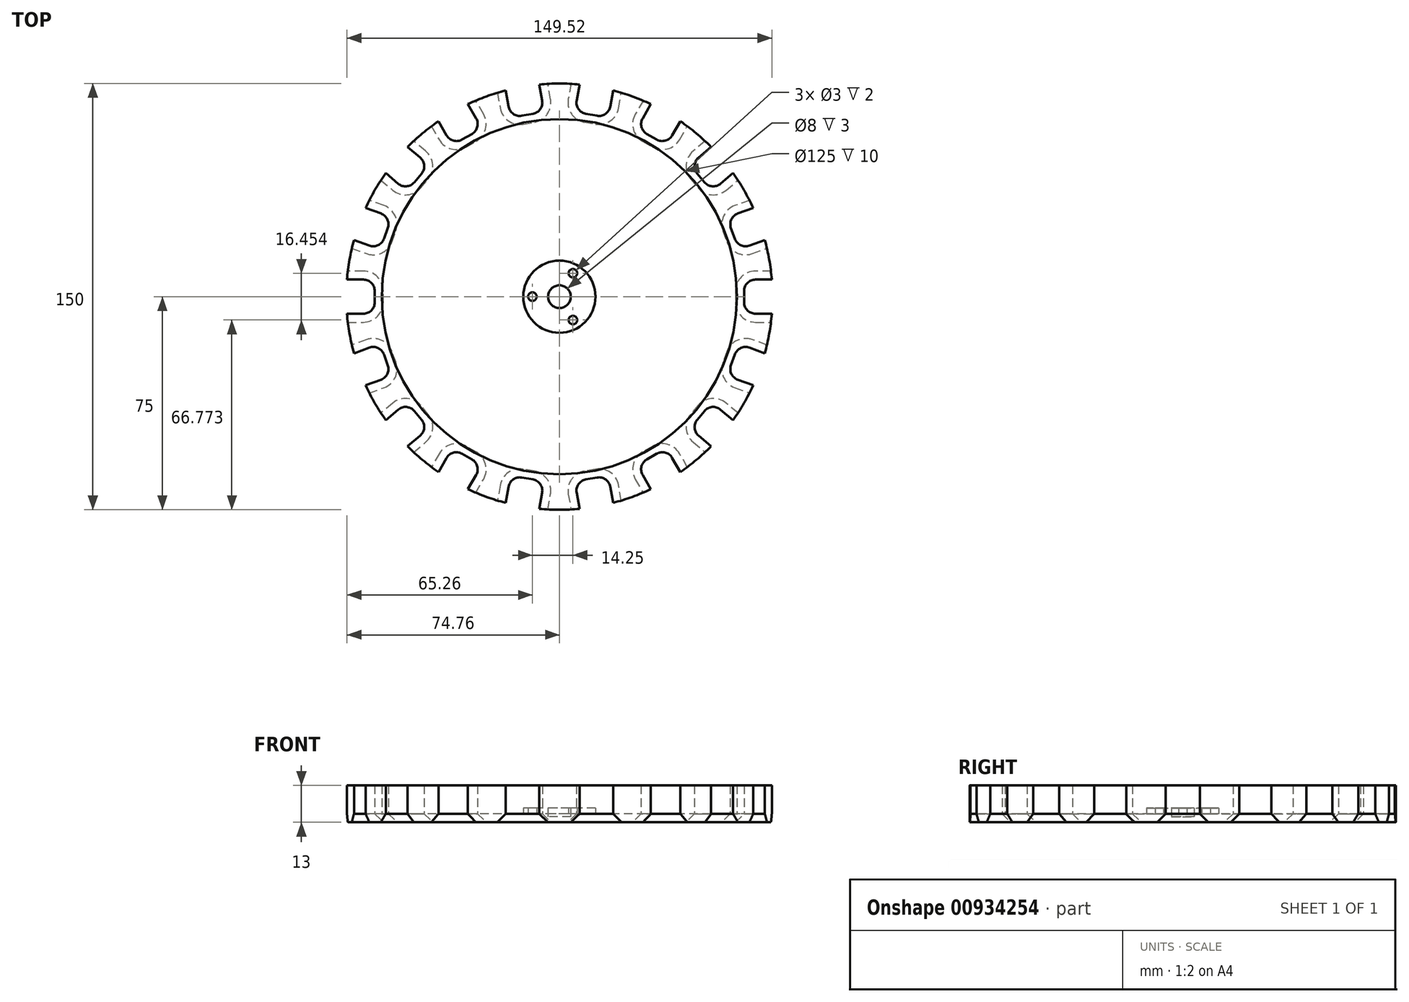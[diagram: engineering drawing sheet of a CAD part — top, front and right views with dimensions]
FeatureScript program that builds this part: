
annotation { "Feature Type Name" : "Feature", "Feature Type Description" : "" }
export const myFeature = defineFeature(function(context is Context, id is Id, definition is map)
    precondition{}
    {
        {
            var Q0;
            Q0=qCreatedBy(makeId("Top.planeOp"),FACE);
            var sketch = newSketch(context, id + "F0", { "sketchPlane" : qUnion([Q0])});
            skCircle(sketch, "E0", {"center": v(0, 0) * mm, "radius": 75 * mm});
            skCircle(sketch, "E1", {"center": v(0, 0) * mm, "radius": 62.5 * mm});
            skLineSegment(sketch, "E2", {"start": v(0, 0) * mm, "end": v(-124.02, 0) * mm, "construction": true});
            skPoint(sketch, "E3", {"position": v(-75, 0) * mm});
            skLineSegment(sketch, "E4.bottom", {"start": v(-75, -6) * mm, "end": v(-69, -6) * mm});
            skLineSegment(sketch, "E4.top", {"start": v(-75, 6) * mm, "end": v(-69, 6) * mm});
            skLineSegment(sketch, "E4.left", {"start": v(-75, -6) * mm, "end": v(-75, 6) * mm});
            skLineSegment(sketch, "E4.right", {"start": v(-65, -2) * mm, "end": v(-65, 2) * mm});
            skPoint(sketch, "E4.middle", {"position": v(-70, 0) * mm});
            skPoint(sketch, "E5.visualSharp", {"position": v(-65, 6) * mm});
            skArc(sketch, "E5.filletArc", {"start": v(-65, 2) * mm, "mid": v(-66.17, 4.83) * mm, "end": v(-69, 6) * mm});
            skPoint(sketch, "E6.visualSharp", {"position": v(-65, -6) * mm});
            skArc(sketch, "E6.filletArc", {"start": v(-69, -6) * mm, "mid": v(-66.17, -4.83) * mm, "end": v(-65, -2) * mm});
            skPoint(sketch, "E7.center", {"position": v(1.56, 0) * mm});
            skCircle(sketch, "E8", {"center": v(0, 0) * mm, "radius": 4 * mm});
            skCircle(sketch, "E9", {"center": v(0, 0) * mm, "radius": 12.7 * mm});
            skCircle(sketch, "E10", {"center": v(0, 0) * mm, "radius": 9.5 * mm, "construction": true});
            skCircle(sketch, "E11", {"center": v(-9.5, 0) * mm, "radius": 1.5 * mm});
            skCircle(sketch, "E12.1.0", {"center": v(-4.75, -8.23) * mm, "radius": 1.5 * mm});
            skCircle(sketch, "E12.2.0", {"center": v(4.75, -8.23) * mm, "radius": 1.5 * mm});
            skCircle(sketch, "E12.3.0", {"center": v(9.5, 0) * mm, "radius": 1.5 * mm});
            skCircle(sketch, "E12.4.0", {"center": v(4.75, 8.23) * mm, "radius": 1.5 * mm});
            skCircle(sketch, "E12.5.0", {"center": v(-4.75, 8.23) * mm, "radius": 1.5 * mm});
            skPoint(sketch, "E13.1.0", {"position": v(-63.13, -16.6) * mm});
            skPoint(sketch, "E13.1.1", {"position": v(-70.48, -25.65) * mm});
            skPoint(sketch, "E13.1.2", {"position": v(-59.03, -27.87) * mm});
            skPoint(sketch, "E13.1.3", {"position": v(-65.78, -23.94) * mm});
            skArc(sketch, "E13.1.4", {"start": v(-62.79, -29.24) * mm, "mid": v(-60.53, -27.17) * mm, "end": v(-60.4, -24.11) * mm});
            skArc(sketch, "E13.1.5", {"start": v(-61.76, -20.35) * mm, "mid": v(-63.83, -18.1) * mm, "end": v(-66.9, -17.96) * mm});
            skLineSegment(sketch, "E13.1.6", {"start": v(-68.42, -31.29) * mm, "end": v(-72.53, -20.01) * mm});
            skLineSegment(sketch, "E13.1.7", {"start": v(-60.4, -24.11) * mm, "end": v(-61.76, -20.35) * mm});
            skLineSegment(sketch, "E13.1.8", {"start": v(-72.53, -20.01) * mm, "end": v(-66.9, -17.96) * mm});
            skLineSegment(sketch, "E13.1.9", {"start": v(-68.42, -31.29) * mm, "end": v(-62.79, -29.24) * mm});
            skPoint(sketch, "E13.2.0", {"position": v(-53.65, -37.18) * mm});
            skPoint(sketch, "E13.2.1", {"position": v(-57.45, -48.2) * mm});
            skPoint(sketch, "E13.2.2", {"position": v(-45.94, -46.38) * mm});
            skPoint(sketch, "E13.2.3", {"position": v(-53.62, -45) * mm});
            skArc(sketch, "E13.2.4", {"start": v(-49, -48.95) * mm, "mid": v(-47.59, -46.23) * mm, "end": v(-48.5, -43.31) * mm});
            skArc(sketch, "E13.2.5", {"start": v(-51.08, -40.25) * mm, "mid": v(-53.8, -38.84) * mm, "end": v(-56.71, -39.76) * mm});
            skLineSegment(sketch, "E13.2.6", {"start": v(-53.6, -52.8) * mm, "end": v(-61.31, -43.61) * mm});
            skLineSegment(sketch, "E13.2.7", {"start": v(-48.5, -43.31) * mm, "end": v(-51.08, -40.25) * mm});
            skLineSegment(sketch, "E13.2.8", {"start": v(-61.31, -43.61) * mm, "end": v(-56.71, -39.76) * mm});
            skLineSegment(sketch, "E13.2.9", {"start": v(-53.6, -52.8) * mm, "end": v(-49, -48.95) * mm});
            skPoint(sketch, "E13.3.0", {"position": v(-37.7, -53.3) * mm});
            skPoint(sketch, "E13.3.1", {"position": v(-37.5, -64.95) * mm});
            skPoint(sketch, "E13.3.2", {"position": v(-27.3, -59.3) * mm});
            skPoint(sketch, "E13.3.3", {"position": v(-35, -60.62) * mm});
            skArc(sketch, "E13.3.4", {"start": v(-29.3, -62.76) * mm, "mid": v(-28.9, -59.72) * mm, "end": v(-30.77, -57.3) * mm});
            skArc(sketch, "E13.3.5", {"start": v(-34.23, -55.3) * mm, "mid": v(-37.27, -54.9) * mm, "end": v(-39.7, -56.76) * mm});
            skLineSegment(sketch, "E13.3.6", {"start": v(-32.3, -67.95) * mm, "end": v(-42.7, -61.95) * mm});
            skLineSegment(sketch, "E13.3.7", {"start": v(-30.77, -57.3) * mm, "end": v(-34.23, -55.3) * mm});
            skLineSegment(sketch, "E13.3.8", {"start": v(-42.7, -61.95) * mm, "end": v(-39.7, -56.76) * mm});
            skLineSegment(sketch, "E13.3.9", {"start": v(-32.3, -67.95) * mm, "end": v(-29.3, -62.76) * mm});
            skPoint(sketch, "E13.4.0", {"position": v(-17.2, -62.97) * mm});
            skPoint(sketch, "E13.4.1", {"position": v(-13.02, -73.86) * mm});
            skPoint(sketch, "E13.4.2", {"position": v(-5.38, -65.05) * mm});
            skPoint(sketch, "E13.4.3", {"position": v(-12.16, -68.94) * mm});
            skArc(sketch, "E13.4.4", {"start": v(-6.07, -69) * mm, "mid": v(-6.74, -66) * mm, "end": v(-9.32, -64.36) * mm});
            skArc(sketch, "E13.4.5", {"start": v(-13.26, -63.67) * mm, "mid": v(-16.25, -64.33) * mm, "end": v(-17.9, -66.9) * mm});
            skLineSegment(sketch, "E13.4.6", {"start": v(-7.11, -74.9) * mm, "end": v(-18.93, -72.82) * mm});
            skLineSegment(sketch, "E13.4.7", {"start": v(-9.32, -64.36) * mm, "end": v(-13.26, -63.67) * mm});
            skLineSegment(sketch, "E13.4.8", {"start": v(-18.93, -72.82) * mm, "end": v(-17.9, -66.9) * mm});
            skLineSegment(sketch, "E13.4.9", {"start": v(-7.11, -74.9) * mm, "end": v(-6.07, -69) * mm});
            skPoint(sketch, "E13.5.0", {"position": v(5.38, -65.05) * mm});
            skPoint(sketch, "E13.5.1", {"position": v(13.02, -73.86) * mm});
            skPoint(sketch, "E13.5.2", {"position": v(17.2, -62.97) * mm});
            skPoint(sketch, "E13.5.3", {"position": v(12.16, -68.94) * mm});
            skArc(sketch, "E13.5.4", {"start": v(17.9, -66.9) * mm, "mid": v(16.25, -64.33) * mm, "end": v(13.26, -63.67) * mm});
            skArc(sketch, "E13.5.5", {"start": v(9.32, -64.36) * mm, "mid": v(6.74, -66) * mm, "end": v(6.07, -69) * mm});
            skLineSegment(sketch, "E13.5.6", {"start": v(18.93, -72.82) * mm, "end": v(7.11, -74.9) * mm});
            skLineSegment(sketch, "E13.5.7", {"start": v(13.26, -63.67) * mm, "end": v(9.32, -64.36) * mm});
            skLineSegment(sketch, "E13.5.8", {"start": v(7.11, -74.9) * mm, "end": v(6.07, -69) * mm});
            skLineSegment(sketch, "E13.5.9", {"start": v(18.93, -72.82) * mm, "end": v(17.9, -66.9) * mm});
            skPoint(sketch, "E13.6.0", {"position": v(27.3, -59.3) * mm});
            skPoint(sketch, "E13.6.1", {"position": v(37.5, -64.95) * mm});
            skPoint(sketch, "E13.6.2", {"position": v(37.7, -53.3) * mm});
            skPoint(sketch, "E13.6.3", {"position": v(35, -60.62) * mm});
            skArc(sketch, "E13.6.4", {"start": v(39.7, -56.76) * mm, "mid": v(37.27, -54.9) * mm, "end": v(34.23, -55.3) * mm});
            skArc(sketch, "E13.6.5", {"start": v(30.77, -57.3) * mm, "mid": v(28.9, -59.72) * mm, "end": v(29.3, -62.76) * mm});
            skLineSegment(sketch, "E13.6.6", {"start": v(42.7, -61.95) * mm, "end": v(32.3, -67.95) * mm});
            skLineSegment(sketch, "E13.6.7", {"start": v(34.23, -55.3) * mm, "end": v(30.77, -57.3) * mm});
            skLineSegment(sketch, "E13.6.8", {"start": v(32.3, -67.95) * mm, "end": v(29.3, -62.76) * mm});
            skLineSegment(sketch, "E13.6.9", {"start": v(42.7, -61.95) * mm, "end": v(39.7, -56.76) * mm});
            skPoint(sketch, "E13.7.0", {"position": v(45.94, -46.38) * mm});
            skPoint(sketch, "E13.7.1", {"position": v(57.45, -48.2) * mm});
            skPoint(sketch, "E13.7.2", {"position": v(53.65, -37.18) * mm});
            skPoint(sketch, "E13.7.3", {"position": v(53.62, -45) * mm});
            skArc(sketch, "E13.7.4", {"start": v(56.71, -39.76) * mm, "mid": v(53.8, -38.84) * mm, "end": v(51.08, -40.25) * mm});
            skArc(sketch, "E13.7.5", {"start": v(48.5, -43.31) * mm, "mid": v(47.59, -46.23) * mm, "end": v(49, -48.95) * mm});
            skLineSegment(sketch, "E13.7.6", {"start": v(61.31, -43.61) * mm, "end": v(53.6, -52.8) * mm});
            skLineSegment(sketch, "E13.7.7", {"start": v(51.08, -40.25) * mm, "end": v(48.5, -43.31) * mm});
            skLineSegment(sketch, "E13.7.8", {"start": v(53.6, -52.8) * mm, "end": v(49, -48.95) * mm});
            skLineSegment(sketch, "E13.7.9", {"start": v(61.31, -43.61) * mm, "end": v(56.71, -39.76) * mm});
            skPoint(sketch, "E13.8.0", {"position": v(59.03, -27.87) * mm});
            skPoint(sketch, "E13.8.1", {"position": v(70.48, -25.65) * mm});
            skPoint(sketch, "E13.8.2", {"position": v(63.13, -16.6) * mm});
            skPoint(sketch, "E13.8.3", {"position": v(65.78, -23.94) * mm});
            skArc(sketch, "E13.8.4", {"start": v(66.9, -17.96) * mm, "mid": v(63.83, -18.1) * mm, "end": v(61.76, -20.35) * mm});
            skArc(sketch, "E13.8.5", {"start": v(60.4, -24.11) * mm, "mid": v(60.53, -27.17) * mm, "end": v(62.79, -29.24) * mm});
            skLineSegment(sketch, "E13.8.6", {"start": v(72.53, -20.01) * mm, "end": v(68.42, -31.29) * mm});
            skLineSegment(sketch, "E13.8.7", {"start": v(61.76, -20.35) * mm, "end": v(60.4, -24.11) * mm});
            skLineSegment(sketch, "E13.8.8", {"start": v(68.42, -31.29) * mm, "end": v(62.79, -29.24) * mm});
            skLineSegment(sketch, "E13.8.9", {"start": v(72.53, -20.01) * mm, "end": v(66.9, -17.96) * mm});
            skPoint(sketch, "E13.9.0", {"position": v(65, -6) * mm});
            skPoint(sketch, "E13.9.1", {"position": v(75, 0) * mm});
            skPoint(sketch, "E13.9.2", {"position": v(65, 6) * mm});
            skPoint(sketch, "E13.9.3", {"position": v(70, 0) * mm});
            skArc(sketch, "E13.9.4", {"start": v(69, 6) * mm, "mid": v(66.17, 4.83) * mm, "end": v(65, 2) * mm});
            skArc(sketch, "E13.9.5", {"start": v(65, -2) * mm, "mid": v(66.17, -4.83) * mm, "end": v(69, -6) * mm});
            skLineSegment(sketch, "E13.9.6", {"start": v(75, 6) * mm, "end": v(75, -6) * mm});
            skLineSegment(sketch, "E13.9.7", {"start": v(65, 2) * mm, "end": v(65, -2) * mm});
            skLineSegment(sketch, "E13.9.8", {"start": v(75, -6) * mm, "end": v(69, -6) * mm});
            skLineSegment(sketch, "E13.9.9", {"start": v(75, 6) * mm, "end": v(69, 6) * mm});
            skPoint(sketch, "E13.10.0", {"position": v(63.13, 16.6) * mm});
            skPoint(sketch, "E13.10.1", {"position": v(70.48, 25.65) * mm});
            skPoint(sketch, "E13.10.2", {"position": v(59.03, 27.87) * mm});
            skPoint(sketch, "E13.10.3", {"position": v(65.78, 23.94) * mm});
            skArc(sketch, "E13.10.4", {"start": v(62.79, 29.24) * mm, "mid": v(60.53, 27.17) * mm, "end": v(60.4, 24.11) * mm});
            skArc(sketch, "E13.10.5", {"start": v(61.76, 20.35) * mm, "mid": v(63.83, 18.1) * mm, "end": v(66.9, 17.96) * mm});
            skLineSegment(sketch, "E13.10.6", {"start": v(68.42, 31.29) * mm, "end": v(72.53, 20.01) * mm});
            skLineSegment(sketch, "E13.10.7", {"start": v(60.4, 24.11) * mm, "end": v(61.76, 20.35) * mm});
            skLineSegment(sketch, "E13.10.8", {"start": v(72.53, 20.01) * mm, "end": v(66.9, 17.96) * mm});
            skLineSegment(sketch, "E13.10.9", {"start": v(68.42, 31.29) * mm, "end": v(62.79, 29.24) * mm});
            skPoint(sketch, "E13.11.0", {"position": v(53.65, 37.18) * mm});
            skPoint(sketch, "E13.11.1", {"position": v(57.45, 48.2) * mm});
            skPoint(sketch, "E13.11.2", {"position": v(45.94, 46.38) * mm});
            skPoint(sketch, "E13.11.3", {"position": v(53.62, 45) * mm});
            skArc(sketch, "E13.11.4", {"start": v(49, 48.95) * mm, "mid": v(47.59, 46.23) * mm, "end": v(48.5, 43.31) * mm});
            skArc(sketch, "E13.11.5", {"start": v(51.08, 40.25) * mm, "mid": v(53.8, 38.84) * mm, "end": v(56.71, 39.76) * mm});
            skLineSegment(sketch, "E13.11.6", {"start": v(53.6, 52.8) * mm, "end": v(61.31, 43.61) * mm});
            skLineSegment(sketch, "E13.11.7", {"start": v(48.5, 43.31) * mm, "end": v(51.08, 40.25) * mm});
            skLineSegment(sketch, "E13.11.8", {"start": v(61.31, 43.61) * mm, "end": v(56.71, 39.76) * mm});
            skLineSegment(sketch, "E13.11.9", {"start": v(53.6, 52.8) * mm, "end": v(49, 48.95) * mm});
            skPoint(sketch, "E13.12.0", {"position": v(37.7, 53.3) * mm});
            skPoint(sketch, "E13.12.1", {"position": v(37.5, 64.95) * mm});
            skPoint(sketch, "E13.12.2", {"position": v(27.3, 59.3) * mm});
            skPoint(sketch, "E13.12.3", {"position": v(35, 60.62) * mm});
            skArc(sketch, "E13.12.4", {"start": v(29.3, 62.76) * mm, "mid": v(28.9, 59.72) * mm, "end": v(30.77, 57.3) * mm});
            skArc(sketch, "E13.12.5", {"start": v(34.23, 55.3) * mm, "mid": v(37.27, 54.9) * mm, "end": v(39.7, 56.76) * mm});
            skLineSegment(sketch, "E13.12.6", {"start": v(32.3, 67.95) * mm, "end": v(42.7, 61.95) * mm});
            skLineSegment(sketch, "E13.12.7", {"start": v(30.77, 57.3) * mm, "end": v(34.23, 55.3) * mm});
            skLineSegment(sketch, "E13.12.8", {"start": v(42.7, 61.95) * mm, "end": v(39.7, 56.76) * mm});
            skLineSegment(sketch, "E13.12.9", {"start": v(32.3, 67.95) * mm, "end": v(29.3, 62.76) * mm});
            skPoint(sketch, "E13.13.0", {"position": v(17.2, 62.97) * mm});
            skPoint(sketch, "E13.13.1", {"position": v(13.02, 73.86) * mm});
            skPoint(sketch, "E13.13.2", {"position": v(5.38, 65.05) * mm});
            skPoint(sketch, "E13.13.3", {"position": v(12.16, 68.94) * mm});
            skArc(sketch, "E13.13.4", {"start": v(6.07, 69) * mm, "mid": v(6.74, 66) * mm, "end": v(9.32, 64.36) * mm});
            skArc(sketch, "E13.13.5", {"start": v(13.26, 63.67) * mm, "mid": v(16.25, 64.33) * mm, "end": v(17.9, 66.9) * mm});
            skLineSegment(sketch, "E13.13.6", {"start": v(7.11, 74.9) * mm, "end": v(18.93, 72.82) * mm});
            skLineSegment(sketch, "E13.13.7", {"start": v(9.32, 64.36) * mm, "end": v(13.26, 63.67) * mm});
            skLineSegment(sketch, "E13.13.8", {"start": v(18.93, 72.82) * mm, "end": v(17.9, 66.9) * mm});
            skLineSegment(sketch, "E13.13.9", {"start": v(7.11, 74.9) * mm, "end": v(6.07, 69) * mm});
            skPoint(sketch, "E13.14.0", {"position": v(-5.38, 65.05) * mm});
            skPoint(sketch, "E13.14.1", {"position": v(-13.02, 73.86) * mm});
            skPoint(sketch, "E13.14.2", {"position": v(-17.2, 62.97) * mm});
            skPoint(sketch, "E13.14.3", {"position": v(-12.16, 68.94) * mm});
            skArc(sketch, "E13.14.4", {"start": v(-17.9, 66.9) * mm, "mid": v(-16.25, 64.33) * mm, "end": v(-13.26, 63.67) * mm});
            skArc(sketch, "E13.14.5", {"start": v(-9.32, 64.36) * mm, "mid": v(-6.74, 66) * mm, "end": v(-6.07, 69) * mm});
            skLineSegment(sketch, "E13.14.6", {"start": v(-18.93, 72.82) * mm, "end": v(-7.11, 74.9) * mm});
            skLineSegment(sketch, "E13.14.7", {"start": v(-13.26, 63.67) * mm, "end": v(-9.32, 64.36) * mm});
            skLineSegment(sketch, "E13.14.8", {"start": v(-7.11, 74.9) * mm, "end": v(-6.07, 69) * mm});
            skLineSegment(sketch, "E13.14.9", {"start": v(-18.93, 72.82) * mm, "end": v(-17.9, 66.9) * mm});
            skPoint(sketch, "E13.15.0", {"position": v(-27.3, 59.3) * mm});
            skPoint(sketch, "E13.15.1", {"position": v(-37.5, 64.95) * mm});
            skPoint(sketch, "E13.15.2", {"position": v(-37.7, 53.3) * mm});
            skPoint(sketch, "E13.15.3", {"position": v(-35, 60.62) * mm});
            skArc(sketch, "E13.15.4", {"start": v(-39.7, 56.76) * mm, "mid": v(-37.27, 54.9) * mm, "end": v(-34.23, 55.3) * mm});
            skArc(sketch, "E13.15.5", {"start": v(-30.77, 57.3) * mm, "mid": v(-28.9, 59.72) * mm, "end": v(-29.3, 62.76) * mm});
            skLineSegment(sketch, "E13.15.6", {"start": v(-42.7, 61.95) * mm, "end": v(-32.3, 67.95) * mm});
            skLineSegment(sketch, "E13.15.7", {"start": v(-34.23, 55.3) * mm, "end": v(-30.77, 57.3) * mm});
            skLineSegment(sketch, "E13.15.8", {"start": v(-32.3, 67.95) * mm, "end": v(-29.3, 62.76) * mm});
            skLineSegment(sketch, "E13.15.9", {"start": v(-42.7, 61.95) * mm, "end": v(-39.7, 56.76) * mm});
            skPoint(sketch, "E13.16.0", {"position": v(-45.94, 46.38) * mm});
            skPoint(sketch, "E13.16.1", {"position": v(-57.45, 48.2) * mm});
            skPoint(sketch, "E13.16.2", {"position": v(-53.65, 37.18) * mm});
            skPoint(sketch, "E13.16.3", {"position": v(-53.62, 45) * mm});
            skArc(sketch, "E13.16.4", {"start": v(-56.71, 39.76) * mm, "mid": v(-53.8, 38.84) * mm, "end": v(-51.08, 40.25) * mm});
            skArc(sketch, "E13.16.5", {"start": v(-48.5, 43.31) * mm, "mid": v(-47.59, 46.23) * mm, "end": v(-49, 48.95) * mm});
            skLineSegment(sketch, "E13.16.6", {"start": v(-61.31, 43.61) * mm, "end": v(-53.6, 52.8) * mm});
            skLineSegment(sketch, "E13.16.7", {"start": v(-51.08, 40.25) * mm, "end": v(-48.5, 43.31) * mm});
            skLineSegment(sketch, "E13.16.8", {"start": v(-53.6, 52.8) * mm, "end": v(-49, 48.95) * mm});
            skLineSegment(sketch, "E13.16.9", {"start": v(-61.31, 43.61) * mm, "end": v(-56.71, 39.76) * mm});
            skPoint(sketch, "E13.17.0", {"position": v(-59.03, 27.87) * mm});
            skPoint(sketch, "E13.17.1", {"position": v(-70.48, 25.65) * mm});
            skPoint(sketch, "E13.17.2", {"position": v(-63.13, 16.6) * mm});
            skPoint(sketch, "E13.17.3", {"position": v(-65.78, 23.94) * mm});
            skArc(sketch, "E13.17.4", {"start": v(-66.9, 17.96) * mm, "mid": v(-63.83, 18.1) * mm, "end": v(-61.76, 20.35) * mm});
            skArc(sketch, "E13.17.5", {"start": v(-60.4, 24.11) * mm, "mid": v(-60.53, 27.17) * mm, "end": v(-62.79, 29.24) * mm});
            skLineSegment(sketch, "E13.17.6", {"start": v(-72.53, 20.01) * mm, "end": v(-68.42, 31.29) * mm});
            skLineSegment(sketch, "E13.17.7", {"start": v(-61.76, 20.35) * mm, "end": v(-60.4, 24.11) * mm});
            skLineSegment(sketch, "E13.17.8", {"start": v(-68.42, 31.29) * mm, "end": v(-62.79, 29.24) * mm});
            skLineSegment(sketch, "E13.17.9", {"start": v(-72.53, 20.01) * mm, "end": v(-66.9, 17.96) * mm});
            skSolve(sketch);
        }
        {
            var Q0;
            Q0=makeQuery(id+"F0.imprint","IMPRINT",FACE,{"disambiguationData":[TD([[makeQuery(id+"F0.imprint","IMPRINT",EDGE,{"derivedFrom":sQuery(id+"F0.wireOp",EDGE,"E1")}),1.0]])]});
            var Q1;
            Q1=makeQuery(id+"F0.imprint","IMPRINT",FACE,{"disambiguationData":[TD([[makeQuery(id+"F0.imprint","IMPRINT",EDGE,{"derivedFrom":sQuery(id+"F0.wireOp",EDGE,"E8")}),-1.0]])]});
            var Q2;
            Q2=makeQuery(id+"F0.imprint","IMPRINT",FACE,{"disambiguationData":[TD([[makeQuery(id+"F0.imprint","IMPRINT",EDGE,{"derivedFrom":sQuery(id+"F0.wireOp",EDGE,"E12.3.0")}),1.0]])]});
            var Q3;
            Q3=makeQuery(id+"F0.imprint","IMPRINT",FACE,{"disambiguationData":[TD([[makeQuery(id+"F0.imprint","IMPRINT",EDGE,{"derivedFrom":sQuery(id+"F0.wireOp",EDGE,"E12.4.0")}),1.0]])]});
            var Q4;
            Q4=makeQuery(id+"F0.imprint","IMPRINT",FACE,{"disambiguationData":[TD([[makeQuery(id+"F0.imprint","IMPRINT",EDGE,{"derivedFrom":sQuery(id+"F0.wireOp",EDGE,"E12.5.0")}),1.0]])]});
            var Q5;
            Q5=makeQuery(id+"F0.imprint","IMPRINT",FACE,{"disambiguationData":[TD([[makeQuery(id+"F0.imprint","IMPRINT",EDGE,{"derivedFrom":sQuery(id+"F0.wireOp",EDGE,"E11")}),1.0]])]});
            var Q6;
            Q6=makeQuery(id+"F0.imprint","IMPRINT",FACE,{"disambiguationData":[TD([[makeQuery(id+"F0.imprint","IMPRINT",EDGE,{"derivedFrom":sQuery(id+"F0.wireOp",EDGE,"E12.1.0")}),1.0]])]});
            var Q7;
            Q7=makeQuery(id+"F0.imprint","IMPRINT",FACE,{"disambiguationData":[TD([[makeQuery(id+"F0.imprint","IMPRINT",EDGE,{"derivedFrom":sQuery(id+"F0.wireOp",EDGE,"E12.2.0")}),1.0]])]});
            extrude(context, id + "F1", {"entities" : qUnion([Q0, Q1, Q2, Q3, Q4, Q5, Q6, Q7]), "depth" : 3 * mm, "offsetDistance" : 25 * mm});
        }
        {
            var Q0;
            Q0=makeQuery(id+"F0.imprint","IMPRINT",FACE,{"disambiguationData":[TD([[makeQuery(id+"F0.imprint","IMPRINT",EDGE,{"derivedFrom":sQuery(id+"F0.wireOp",EDGE,"E1")}),-1.0]])]});
            extrude(context, id + "F2", {"entities" : qUnion([Q0]), "operationType" : NewBodyOperationType.ADD, "depth" : 13 * mm, "offsetDistance" : 25 * mm});
        }
        {
            var Q0;
            Q0=makeQuery(id+"F0.imprint","IMPRINT",FACE,{"disambiguationData":[TD([[makeQuery(id+"F0.imprint","IMPRINT",EDGE,{"derivedFrom":sQuery(id+"F0.wireOp",EDGE,"E8")}),-1.0]])]});
            var Q1;
            Q1=makeQuery(id+"F0.imprint","IMPRINT",FACE,{"disambiguationData":[TD([[makeQuery(id+"F0.imprint","IMPRINT",EDGE,{"derivedFrom":sQuery(id+"F0.wireOp",EDGE,"E12.5.0")}),1.0]])]});
            var Q2;
            Q2=makeQuery(id+"F0.imprint","IMPRINT",FACE,{"disambiguationData":[TD([[makeQuery(id+"F0.imprint","IMPRINT",EDGE,{"derivedFrom":sQuery(id+"F0.wireOp",EDGE,"E12.3.0")}),1.0]])]});
            var Q3;
            Q3=makeQuery(id+"F0.imprint","IMPRINT",FACE,{"disambiguationData":[TD([[makeQuery(id+"F0.imprint","IMPRINT",EDGE,{"derivedFrom":sQuery(id+"F0.wireOp",EDGE,"E12.1.0")}),1.0]])]});
            extrude(context, id + "F3", {"entities" : qUnion([Q0, Q1, Q2, Q3]), "operationType" : NewBodyOperationType.ADD, "depth" : 5 * mm, "offsetDistance" : 25 * mm});
        }
        {
            var Q0;
            Q0=makeQuery(id+"F0.imprint","IMPRINT",FACE,{"disambiguationData":[TD([[makeQuery(id+"F0.imprint","IMPRINT",EDGE,{"derivedFrom":sQuery(id+"F0.wireOp",EDGE,"E8")}),1.0]])]});
            extrude(context, id + "F4", {"entities" : qUnion([Q0]), "operationType" : NewBodyOperationType.ADD, "depth" : 2 * mm, "offsetDistance" : 25 * mm});
        }
        {
            var Q0;
            Q0=makeQuery(id+"F2.opExtrude","CAP_EDGE",EDGE,{"disambiguationData":[OSD([sQuery(id+"F0.wireOp",EDGE,"E13.4.9")])],"isStart":true});
            var Q1;
            Q1=makeQuery(id+"F2.opExtrude","CAP_EDGE",EDGE,{"disambiguationData":[OSD([sQuery(id+"F0.wireOp",EDGE,"E13.3.9")])],"isStart":true});
            var Q2;
            Q2=makeQuery(id+"F2.opExtrude","CAP_EDGE",EDGE,{"disambiguationData":[OSD([sQuery(id+"F0.wireOp",EDGE,"E13.2.9")])],"isStart":true});
            var Q3;
            Q3=makeQuery(id+"F2.opExtrude","CAP_EDGE",EDGE,{"disambiguationData":[OSD([sQuery(id+"F0.wireOp",EDGE,"E13.1.9")])],"isStart":true});
            var Q4;
            Q4=makeQuery(id+"F2.opExtrude","CAP_EDGE",EDGE,{"disambiguationData":[OSD([sQuery(id+"F0.wireOp",EDGE,"E13.17.9")])],"isStart":true});
            var Q5;
            Q5=makeQuery(id+"F2.opExtrude","CAP_EDGE",EDGE,{"disambiguationData":[OSD([sQuery(id+"F0.wireOp",EDGE,"E13.16.9")])],"isStart":true});
            var Q6;
            Q6=makeQuery(id+"F2.opExtrude","CAP_EDGE",EDGE,{"disambiguationData":[OSD([sQuery(id+"F0.wireOp",EDGE,"E13.15.9")])],"isStart":true});
            var Q7;
            Q7=makeQuery(id+"F2.opExtrude","CAP_EDGE",EDGE,{"disambiguationData":[OSD([sQuery(id+"F0.wireOp",EDGE,"E13.14.9")])],"isStart":true});
            var Q8;
            Q8=makeQuery(id+"F2.opExtrude","CAP_EDGE",EDGE,{"disambiguationData":[OSD([sQuery(id+"F0.wireOp",EDGE,"E13.13.9")])],"isStart":true});
            var Q9;
            Q9=makeQuery(id+"F2.opExtrude","CAP_EDGE",EDGE,{"disambiguationData":[OSD([sQuery(id+"F0.wireOp",EDGE,"E13.12.9")])],"isStart":true});
            var Q10;
            Q10=makeQuery(id+"F2.opExtrude","CAP_EDGE",EDGE,{"disambiguationData":[OSD([sQuery(id+"F0.wireOp",EDGE,"E13.11.8")])],"isStart":true});
            var Q11;
            Q11=makeQuery(id+"F2.opExtrude","CAP_EDGE",EDGE,{"disambiguationData":[OSD([sQuery(id+"F0.wireOp",EDGE,"E13.10.9")])],"isStart":true});
            var Q12;
            Q12=makeQuery(id+"F2.opExtrude","CAP_EDGE",EDGE,{"disambiguationData":[OSD([sQuery(id+"F0.wireOp",EDGE,"E13.9.9")])],"isStart":true});
            var Q13;
            Q13=makeQuery(id+"F2.opExtrude","CAP_EDGE",EDGE,{"disambiguationData":[OSD([sQuery(id+"F0.wireOp",EDGE,"E13.8.9")])],"isStart":true});
            var Q14;
            Q14=makeQuery(id+"F2.opExtrude","CAP_EDGE",EDGE,{"disambiguationData":[OSD([sQuery(id+"F0.wireOp",EDGE,"E13.5.8")])],"isStart":true});
            var Q15;
            Q15=makeQuery(id+"F2.opExtrude","CAP_EDGE",EDGE,{"disambiguationData":[OSD([sQuery(id+"F0.wireOp",EDGE,"E13.6.8")])],"isStart":true});
            var Q16;
            Q16=makeQuery(id+"F2.opExtrude","CAP_EDGE",EDGE,{"disambiguationData":[OSD([sQuery(id+"F0.wireOp",EDGE,"E13.7.8")])],"isStart":true});
            var Q17;
            Q17=makeQuery(id+"F2.opExtrude","CAP_EDGE",EDGE,{"disambiguationData":[OSD([sQuery(id+"F0.wireOp",EDGE,"E4.right")])],"isStart":true});
            chamfer(context, id + "F5", {"entities" : qUnion([Q0, Q1, Q2, Q3, Q4, Q5, Q6, Q7, Q8, Q9, Q10, Q11, Q12, Q13, Q14, Q15, Q16, Q17]), "chamferType" : ChamferType.OFFSET_ANGLE, "width" : 3 * mm, "oppositeDirection" : false, "angle" : 45 * degree, "tangentPropagation" : true});
        }
    });
